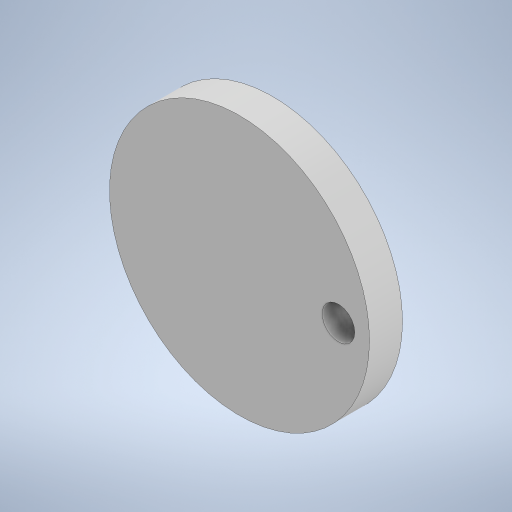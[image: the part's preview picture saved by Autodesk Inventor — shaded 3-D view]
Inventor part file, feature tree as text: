
AUTODESK INVENTOR PART (.ipt)
format: ipt  version: 2024 (Build 280153000, 153)  size: 215,040 bytes
history: native  units: in
note: dims shown in document units (in); Inventor stores cm internally (conversion verified against a paired STEP export)
features: extrude x2, sketch x2
ambient origin geometry x8: Origin, YZ Plane, XZ Plane, XY Plane, X Axis, Y Axis, Z Axis, Center Point
bodies: Solid1 (feature_tree)
feature tree (4):
  extrude  "Extrusion1"  Depth=5.0in TaperAngle=0.0deg
  extrude  "Extrusion2"  Depth=5.0in
  sketch  "Sketch1"  dims[d0=39.3701in d1=5.0in d2=0.0in]
  sketch  "Sketch3"  dims[d3=4.9498in d4=14.988in d5=5.0in d6=0.0in]
